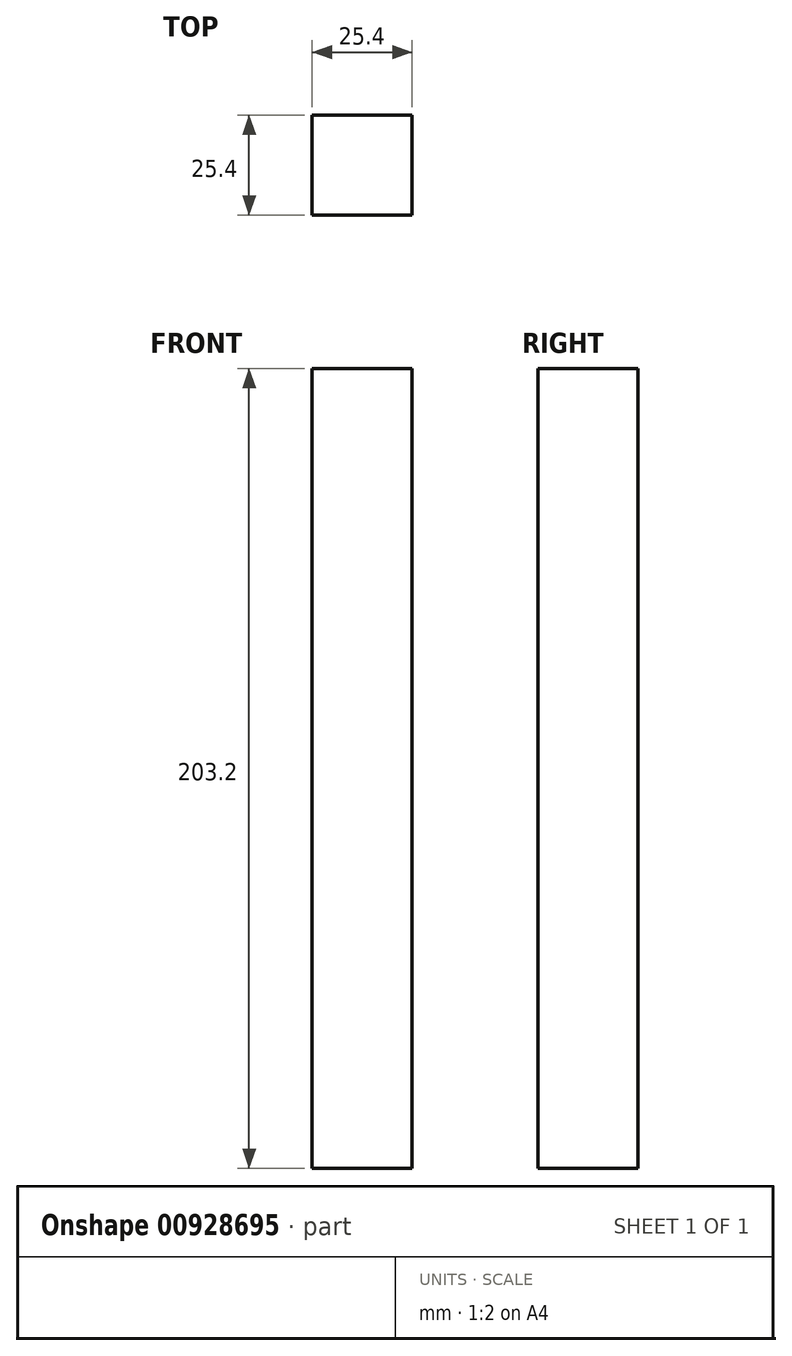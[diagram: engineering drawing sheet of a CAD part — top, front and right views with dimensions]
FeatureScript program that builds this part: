
annotation { "Feature Type Name" : "Feature", "Feature Type Description" : "" }
export const myFeature = defineFeature(function(context is Context, id is Id, definition is map)
    precondition{}
    {
        {
            var Q0;
            Q0=qCreatedBy(makeId("Top.planeOp"),FACE);
            var sketch = newSketch(context, id + "F0", { "sketchPlane" : qUnion([Q0])});
            skLineSegment(sketch, "E0.bottom", {"start": v(0, 0) * mm, "end": v(25.4, 0) * mm});
            skLineSegment(sketch, "E0.top", {"start": v(0, 25.4) * mm, "end": v(25.4, 25.4) * mm});
            skLineSegment(sketch, "E0.left", {"start": v(0, 0) * mm, "end": v(0, 25.4) * mm});
            skLineSegment(sketch, "E0.right", {"start": v(25.4, 0) * mm, "end": v(25.4, 25.4) * mm});
            skSolve(sketch);
        }
        {
            var Q0;
            Q0 = qSketchRegion(id + "F0", true);
            extrude(context, id + "F1", {"entities" : qUnion([Q0]), "depth" : 203.2 * mm, "offsetDistance" : 25.4 * mm});
        }
    });
